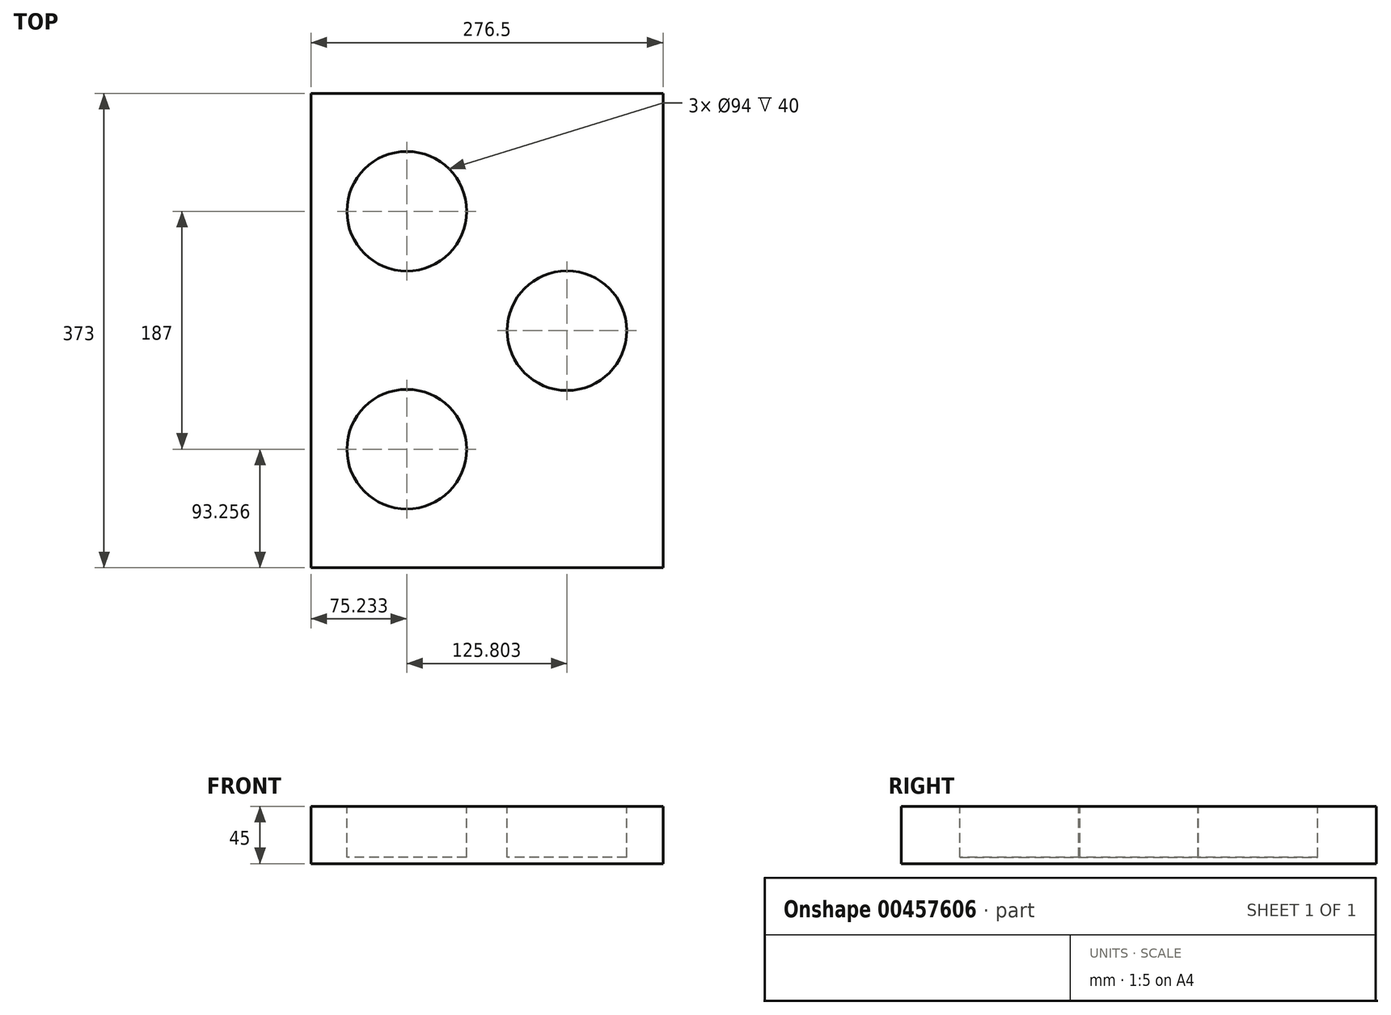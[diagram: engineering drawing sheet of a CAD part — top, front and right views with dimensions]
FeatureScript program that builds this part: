
annotation { "Feature Type Name" : "Feature", "Feature Type Description" : "" }
export const myFeature = defineFeature(function(context is Context, id is Id, definition is map)
    precondition{}
    {
        {
            var Q0;
            Q0=qCreatedBy(makeId("Top.planeOp"),FACE);
            var sketch = newSketch(context, id + "F0", { "sketchPlane" : qUnion([Q0])});
            skLineSegment(sketch, "E0.bottom", {"start": v(138.25, 186.5) * mm, "end": v(-138.25, 186.5) * mm});
            skLineSegment(sketch, "E0.top", {"start": v(138.25, -186.5) * mm, "end": v(-138.25, -186.5) * mm});
            skLineSegment(sketch, "E0.left", {"start": v(138.25, 186.5) * mm, "end": v(138.25, -186.5) * mm});
            skLineSegment(sketch, "E0.right", {"start": v(-138.25, 186.5) * mm, "end": v(-138.25, -186.5) * mm});
            skPoint(sketch, "E0.middle", {"position": v(0, 0) * mm});
            skSolve(sketch);
        }
        {
            var Q0;
            Q0=makeQuery(id+"F0.imprint","IMPRINT",FACE,{"disambiguationData":[TD([[makeQuery(id+"F0.imprint","IMPRINT",EDGE,{"derivedFrom":sQuery(id+"F0.wireOp",EDGE,"E0.bottom")}),1.0]])]});
            var sketch = newSketch(context, id + "F1", { "sketchPlane" : qUnion([Q0])});
            skLineSegment(sketch, "E1", {"start": v(-138.02, 186.76) * mm, "end": v(-63.02, 186.76) * mm, "construction": true});
            skLineSegment(sketch, "E2", {"start": v(-63.02, 186.76) * mm, "end": v(-63.02, 93.76) * mm, "construction": true});
            skCircle(sketch, "E3", {"center": v(-63.02, 93.76) * mm, "radius": 47 * mm});
            skLineSegment(sketch, "E4", {"start": v(137.79, 186.4) * mm, "end": v(62.79, 186.4) * mm, "construction": true});
            skLineSegment(sketch, "E5", {"start": v(62.79, 186.4) * mm, "end": v(62.79, -0.1) * mm, "construction": true});
            skCircle(sketch, "E6", {"center": v(62.79, -0.1) * mm, "radius": 47 * mm});
            skLineSegment(sketch, "E7", {"start": v(-138.02, 186.76) * mm, "end": v(-138.02, 0.26) * mm, "construction": true});
            skLineSegment(sketch, "E8", {"start": v(-138.02, 0.26) * mm, "end": v(138.44, 0.26) * mm, "construction": true});
            skCircle(sketch, "E9.MirrorC", {"center": v(-63.02, -93.24) * mm, "radius": 47 * mm});
            skSolve(sketch);
        }
        {
            var Q0;
            Q0=makeQuery(id+"F0.imprint","IMPRINT",FACE,{"disambiguationData":[TD([[makeQuery(id+"F0.imprint","IMPRINT",EDGE,{"derivedFrom":sQuery(id+"F0.wireOp",EDGE,"E0.bottom")}),1.0]])]});
            extrude(context, id + "F2", {"entities" : qUnion([Q0]), "oppositeDirection" : true, "depth" : 45 * mm});
        }
        {
            var Q0;
            Q0=qSketchRegion(id+"F1",true);
            extrude(context, id + "F3", {"entities" : qUnion([Q0]), "operationType" : NewBodyOperationType.REMOVE, "oppositeDirection" : true, "depth" : 40 * mm});
        }
    });
